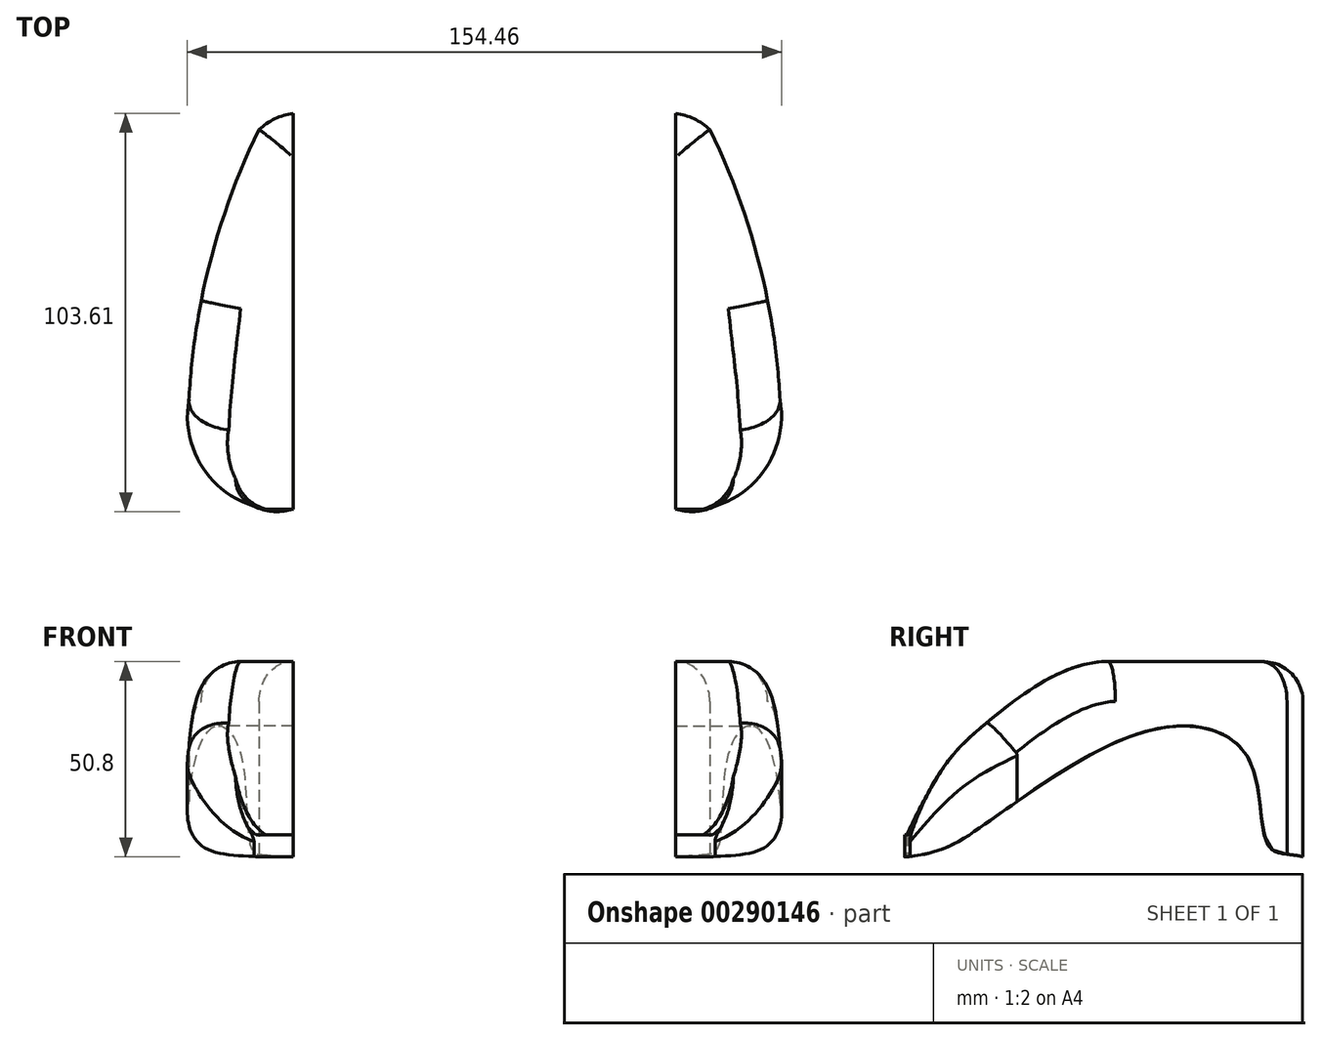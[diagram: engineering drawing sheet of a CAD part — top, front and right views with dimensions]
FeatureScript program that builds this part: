
annotation { "Feature Type Name" : "Feature", "Feature Type Description" : "" }
export const myFeature = defineFeature(function(context is Context, id is Id, definition is map)
    precondition{}
    {
        {
            var Q0;
            Q0=qCreatedBy(makeId("Top.planeOp"),FACE);
            var sketch = newSketch(context, id + "F0", { "sketchPlane" : qUnion([Q0])});
            skLineSegment(sketch, "E0", {"start": v(0, 58.2) * mm, "end": v(-27.09, 58.2) * mm});
            skLineSegment(sketch, "E1", {"start": v(0, -13.7) * mm, "end": v(-21.95, -13.7) * mm});
            skLineSegment(sketch, "E2", {"start": v(-31.65, -19.68) * mm, "end": v(-41.64, -39.37) * mm});
            skArc(sketch, "E3", {"start": v(-21.95, -13.7) * mm, "mid": v(-27.65, -15.32) * mm, "end": v(-31.65, -19.68) * mm});
            skArc(sketch, "E4", {"start": v(-59.94, -45.52) * mm, "mid": v(-49.53, -46.2) * mm, "end": v(-41.64, -39.37) * mm});
            skArc(sketch, "E5", {"start": v(-76.84, -17.66) * mm, "mid": v(-73.68, -34.8) * mm, "end": v(-59.94, -45.52) * mm});
            skArc(sketch, "E6", {"start": v(-58.6, 52.52) * mm, "mid": v(-71.25, 18.35) * mm, "end": v(-76.83, -17.66) * mm});
            skArc(sketch, "E7", {"start": v(-49.74, 56.7) * mm, "mid": v(-54.5, 55.3) * mm, "end": v(-58.6, 52.52) * mm});
            skArc(sketch, "E8", {"start": v(-27.09, 58.2) * mm, "mid": v(-38.44, 57.83) * mm, "end": v(-49.74, 56.7) * mm});
            skArc(sketch, "E9.MirrorCS", {"start": v(27.09, 58.2) * mm, "mid": v(38.44, 57.83) * mm, "end": v(49.74, 56.7) * mm});
            skArc(sketch, "E10.MirrorCS", {"start": v(49.74, 56.7) * mm, "mid": v(54.5, 55.3) * mm, "end": v(58.6, 52.52) * mm});
            skArc(sketch, "E11.MirrorCS", {"start": v(21.95, -13.7) * mm, "mid": v(27.65, -15.32) * mm, "end": v(31.65, -19.68) * mm});
            skLineSegment(sketch, "E12.MirrorCS", {"start": v(0, -13.7) * mm, "end": v(21.95, -13.7) * mm});
            skArc(sketch, "E13.MirrorCS", {"start": v(59.94, -45.52) * mm, "mid": v(49.53, -46.2) * mm, "end": v(41.64, -39.37) * mm});
            skArc(sketch, "E14.MirrorCS", {"start": v(76.84, -17.66) * mm, "mid": v(73.68, -34.8) * mm, "end": v(59.94, -45.52) * mm});
            skArc(sketch, "E15.MirrorCS", {"start": v(58.6, 52.52) * mm, "mid": v(71.25, 18.35) * mm, "end": v(76.83, -17.66) * mm});
            skLineSegment(sketch, "E16.MirrorCS", {"start": v(0, 58.2) * mm, "end": v(27.09, 58.2) * mm});
            skLineSegment(sketch, "E17.MirrorCS", {"start": v(31.65, -19.68) * mm, "end": v(41.64, -39.37) * mm});
            skLineSegment(sketch, "E18.bottom", {"start": v(-36.51, 101.6) * mm, "end": v(36.51, 101.6) * mm});
            skLineSegment(sketch, "E18.top", {"start": v(-36.51, 38.1) * mm, "end": v(36.51, 38.1) * mm});
            skLineSegment(sketch, "E18.left", {"start": v(-36.51, 101.6) * mm, "end": v(-36.51, 38.1) * mm});
            skLineSegment(sketch, "E18.right", {"start": v(36.51, 101.6) * mm, "end": v(36.51, 38.1) * mm});
            skPoint(sketch, "E18.middle", {"position": v(0, 69.85) * mm});
            skLineSegment(sketch, "E19.bottom", {"start": v(-44.45, -25.4) * mm, "end": v(44.45, -25.4) * mm});
            skLineSegment(sketch, "E19.top", {"start": v(-44.45, 38.1) * mm, "end": v(44.45, 38.1) * mm});
            skLineSegment(sketch, "E19.left", {"start": v(-44.45, -25.4) * mm, "end": v(-44.45, 38.1) * mm});
            skLineSegment(sketch, "E19.right", {"start": v(44.45, -25.4) * mm, "end": v(44.45, 38.1) * mm});
            skPoint(sketch, "E19.middle", {"position": v(0, 6.35) * mm});
            skLineSegment(sketch, "E20", {"start": v(-44.45, 38.1) * mm, "end": v(-44.45, 107.95) * mm});
            skLineSegment(sketch, "E21", {"start": v(-44.45, 107.95) * mm, "end": v(44.45, 107.95) * mm});
            skLineSegment(sketch, "E22", {"start": v(44.45, 107.95) * mm, "end": v(44.45, 38.1) * mm});
            skLineSegment(sketch, "E23", {"start": v(-49.74, 56.7) * mm, "end": v(-49.74, -46.26) * mm});
            skLineSegment(sketch, "E24", {"start": v(49.74, 56.7) * mm, "end": v(49.74, -46.26) * mm});
            skSolve(sketch);
        }
        {
            var Q0;
            {var subQ0=sQuery(id+"F0.wireOp",EDGE,"E5");Q0=makeQuery(id+"F0.imprint","IMPRINT",FACE,{"disambiguationData":[TD([[makeQuery(id+"F0.imprint","IMPRINT",EDGE,{"derivedFrom":subQ0}),1.0]])]});}
            extrude(context, id + "F1", {"entities" : qUnion([Q0]), "depth" : 50.8 * mm});
        }
        {
            var Q0;
            Q0=makeQuery(id+"F1.opExtrude","SWEPT_FACE",FACE,{"disambiguationData":[OSD([sQuery(id+"F0.wireOp",EDGE,"E23")])]});
            var sketch = newSketch(context, id + "F2", { "sketchPlane" : qUnion([Q0])});
            skPoint(sketch, "E25", {"position": v(-27.2, 7.62) * mm});
            skPoint(sketch, "E26", {"position": v(17.24, 33.02) * mm});
            skPoint(sketch, "E27", {"position": v(42.64, 25.4) * mm});
            skFitSpline(sketch, "E28", {"points": [v(-46.26, 0) * mm, v(-27.2, 7.62) * mm, v(17.24, 33.02) * mm, v(42.64, 25.4) * mm, v(47.91, 2.54) * mm, v(56.7, 0) * mm], "startDerivative": vector(137.02, 14.8) * mm, "endDerivative": vector(84.94, -23.6) * mm});
            skPoint(sketch, "E29", {"position": v(5.9, 50.8) * mm});
            skFitSpline(sketch, "E30", {"points": [v(-46.26, 5.77) * mm, v(-36.18, 24.12) * mm, v(-24.15, 36) * mm, v(5.9, 50.8) * mm, v(49.1, 24.72) * mm], "startDerivative": vector(45.94, 94.68) * mm, "endDerivative": vector(132.77, -118.88) * mm});
            skLineSegment(sketch, "E31", {"start": v(5.9, 50.8) * mm, "end": v(5.9, 43.82) * mm});
            skSolve(sketch);
        }
        {
            var Q0;
            Q0=makeQuery(id+"F2.imprint","IMPRINT",FACE,{"disambiguationData":[TD([[makeQuery(id+"F2.imprint","IMPRINT",EDGE,{"derivedFrom":sQuery(id+"F2.wireOp",EDGE,"E28")}),-1.0]])]});
            var Q1;
            {var subQ0=sQuery(id+"F2.wireOp",EDGE,"E30");Q1=makeQuery(id+"F2.imprint","IMPRINT",FACE,{"disambiguationData":[TD([[makeQuery(id+"F2.imprint","IMPRINT",EDGE,{"derivedFrom":subQ0}),1.0]])]});}
            extrude(context, id + "F3", {"entities" : qUnion([Q0, Q1]), "operationType" : NewBodyOperationType.REMOVE, "endBound" : BoundingType.THROUGH_ALL, "oppositeDirection" : true, "depth" : 25.4 * mm});
        }
        {
            var Q0;
            Q0=makeQuery(id+"F3.boolean.opBoolean","COPY",FACE,{"derivedFrom":makeQuery(id+"F3.opExtrude","SWEPT_FACE",FACE,{"disambiguationData":[OSD([sQuery(id+"F0.wireOp",EDGE,"E4"),sQuery(id+"F0.wireOp",EDGE,"E23")])]})});
            extrude(context, id + "F4", {"entities" : qUnion([Q0]), "operationType" : NewBodyOperationType.REMOVE, "oppositeDirection" : true, "depth" : 25.4 * mm});
        }
        {
            var Q0;
            Q0=makeQuery(id+"F1.opExtrude","CAP_EDGE",EDGE,{"disambiguationData":[OSD([sQuery(id+"F0.wireOp",EDGE,"E7")])],"isStart":false});
            var Q1;
            Q1=makeQuery(id+"F1.opExtrude","CAP_EDGE",EDGE,{"disambiguationData":[OSD([sQuery(id+"F0.wireOp",EDGE,"E6")])],"isStart":false});
            var Q2;
            Q2=makeQuery(id+"F3.boolean.opBoolean","INTERSECT",EDGE,{"derivedFrom":[makeQuery(id+"F1.opExtrude","SWEPT_FACE",FACE,{"disambiguationData":[OSD([sQuery(id+"F0.wireOp",EDGE,"E6")])]}),makeQuery(id+"F3.opExtrude","SWEPT_FACE",FACE,{"disambiguationData":[OSD([sQuery(id+"F2.wireOp",EDGE,"E30")])]})]});
            var Q3;
            Q3=makeQuery(id+"F3.boolean.opBoolean","INTERSECT",EDGE,{"derivedFrom":[makeQuery(id+"F1.opExtrude","SWEPT_FACE",FACE,{"disambiguationData":[OSD([sQuery(id+"F0.wireOp",EDGE,"E5")])]}),makeQuery(id+"F3.opExtrude","SWEPT_FACE",FACE,{"disambiguationData":[OSD([sQuery(id+"F2.wireOp",EDGE,"E30")])]})]});
            fillet(context, id + "F5", {"entities" : qUnion([Q0, Q1, Q2, Q3]), "radius" : 10.4 * mm, "tangentPropagation" : true, "allowEdgeOverflow" : false});
        }
        {
            var Q0;
            Q0=makeQuery(id+"F3.boolean.opBoolean","INTERSECT",EDGE,{"derivedFrom":[makeQuery(id+"F1.opExtrude","SWEPT_FACE",FACE,{"disambiguationData":[OSD([sQuery(id+"F0.wireOp",EDGE,"E4")])]}),makeQuery(id+"F3.opExtrude","SWEPT_FACE",FACE,{"disambiguationData":[OSD([sQuery(id+"F2.wireOp",EDGE,"E30")])]})]});
            fillet(context, id + "F6", {"entities" : qUnion([Q0]), "radius" : 2.54 * mm, "tangentPropagation" : true, "allowEdgeOverflow" : false});
        }
        {
            var Q0;
            Q0=makeQuery(id+"F1.opExtrude","SWEPT_BODY",BODY,{"disambiguationData":[OSD([sQuery(id+"F0.wireOp",EDGE,"E4"),sQuery(id+"F0.wireOp",EDGE,"E5"),sQuery(id+"F0.wireOp",EDGE,"E6"),sQuery(id+"F0.wireOp",EDGE,"E7"),sQuery(id+"F0.wireOp",EDGE,"E23")])]});
            var Q1;
            Q1=qCreatedBy(makeId("Right.planeOp"),FACE);
            mirror(context, id + "F7", {"entities" : qUnion([Q0]), "mirrorPlane" : qUnion([Q1])});
        }
    });
